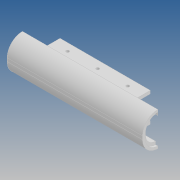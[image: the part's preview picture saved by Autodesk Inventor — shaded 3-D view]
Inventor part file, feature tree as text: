
AUTODESK INVENTOR PART (.ipt)
format: ipt  version: 2020 (Build 240168000, 168)  size: 206,336 bytes
history: native  units: mm
features: extrude x6, sketch x6, other x4, mirror x2, pattern_linear x1, projected_geometry x1
ambient origin geometry x8: Origin, YZ Plane, XZ Plane, XY Plane, X Axis, Y Axis, Z Axis, Center Point
bodies: Body1 (feature_tree)
feature tree (20):
  other  "Твердое тело1"
  extrude  "Выдавливание1"  Depth=180.0mm
  extrude  "Выдавливание2"  Depth=20.0mm
  extrude  "Выдавливание3"  Depth=4.0mm TaperAngle=0.0deg
  pattern_linear  "Прямоуг.массив1"  Spacing1=3.0mm  [1 undecoded]
  extrude  "Выдавливание4"  Depth=180.0mm TaperAngle=0.0deg
  other  "РабПлоскость1"
  extrude  "Выдавливание6"  Depth=4.0mm
  mirror  "Зеркальное отражение4"
  mirror  "Зеркальное отражение2"
  extrude  "Выдавливание5"  Depth=10.0mm
  other  "Толщина1"
  other  "Толщина2"
  sketch  "Эскиз1"
  sketch  "Эскиз2"
  sketch  "Эскиз3"
  sketch  "Эскиз4"
  projected_geometry  "Спроецированная петля1"
  sketch  "Эскиз5"
  sketch  "Эскиз6"
note: 1 required parameter value undecoded (feature->parameter linkage not recoverable at this tier; creation-order binding heuristic only, values carry confidence <= 0.55)
